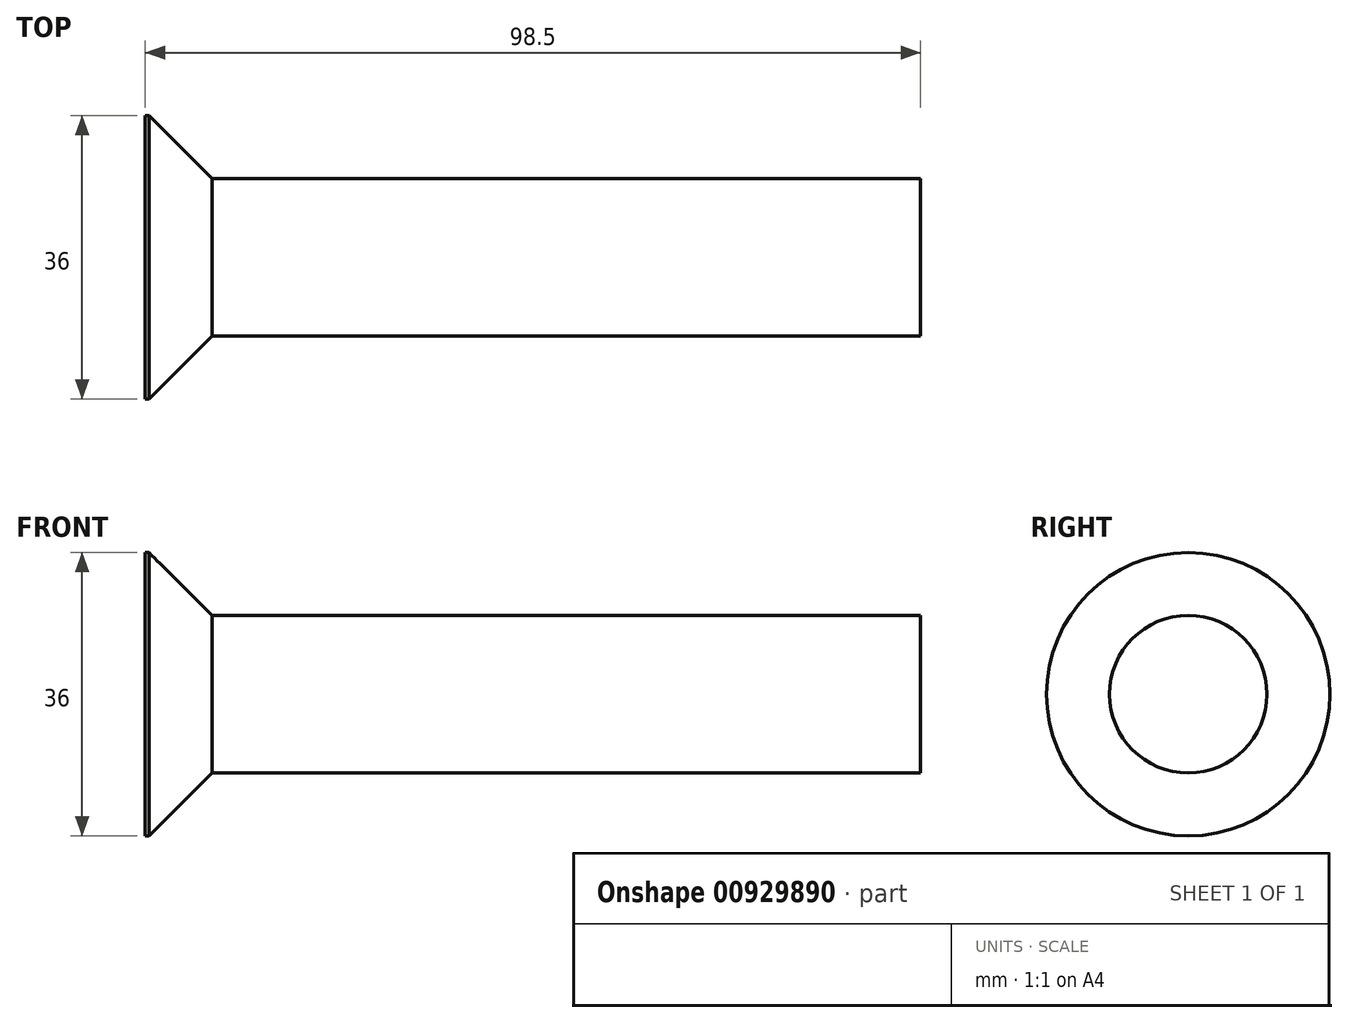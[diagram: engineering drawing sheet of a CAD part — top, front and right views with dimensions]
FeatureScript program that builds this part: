
annotation { "Feature Type Name" : "Feature", "Feature Type Description" : "" }
export const myFeature = defineFeature(function(context is Context, id is Id, definition is map)
    precondition{}
    {
        {
            var Q0;
            Q0=qCreatedBy(makeId("Front.planeOp"),FACE);
            var sketch = newSketch(context, id + "F0", { "sketchPlane" : qUnion([Q0])});
            skLineSegment(sketch, "E0.0", {"start": v(100, 0) * mm, "end": v(100, 10) * mm});
            skLineSegment(sketch, "E1.1", {"start": v(1.5, 18) * mm, "end": v(2, 18) * mm});
            skLineSegment(sketch, "E2", {"start": v(2, 18) * mm, "end": v(10, 10) * mm});
            skLineSegment(sketch, "E3.trimOffspring", {"start": v(10, 10) * mm, "end": v(100, 10) * mm});
            skLineSegment(sketch, "E4", {"start": v(1.5, 0) * mm, "end": v(100, 0) * mm});
            skLineSegment(sketch, "E5.0", {"start": v(1.5, 18) * mm, "end": v(1.5, 0) * mm});
            skSolve(sketch);
        }
        {
            var Q0;
            Q0=makeQuery(id+"F0.imprint","IMPRINT",FACE,{"disambiguationData":[TD([[makeQuery(id+"F0.imprint","IMPRINT",EDGE,{"derivedFrom":sQuery(id+"F0.wireOp",EDGE,"E0.0")}),1.0]])]});
            var Q1;
            Q1=sQuery(id+"F0.wireOp",EDGE,"E4");
            revolve(context, id + "F1", {"surfaceOperationType" : NewSurfaceOperationType.NEW, "entities" : qUnion([Q0]), "axis" : qUnion([Q1]), "revolveType" : RevolveType.FULL});
        }
    });
